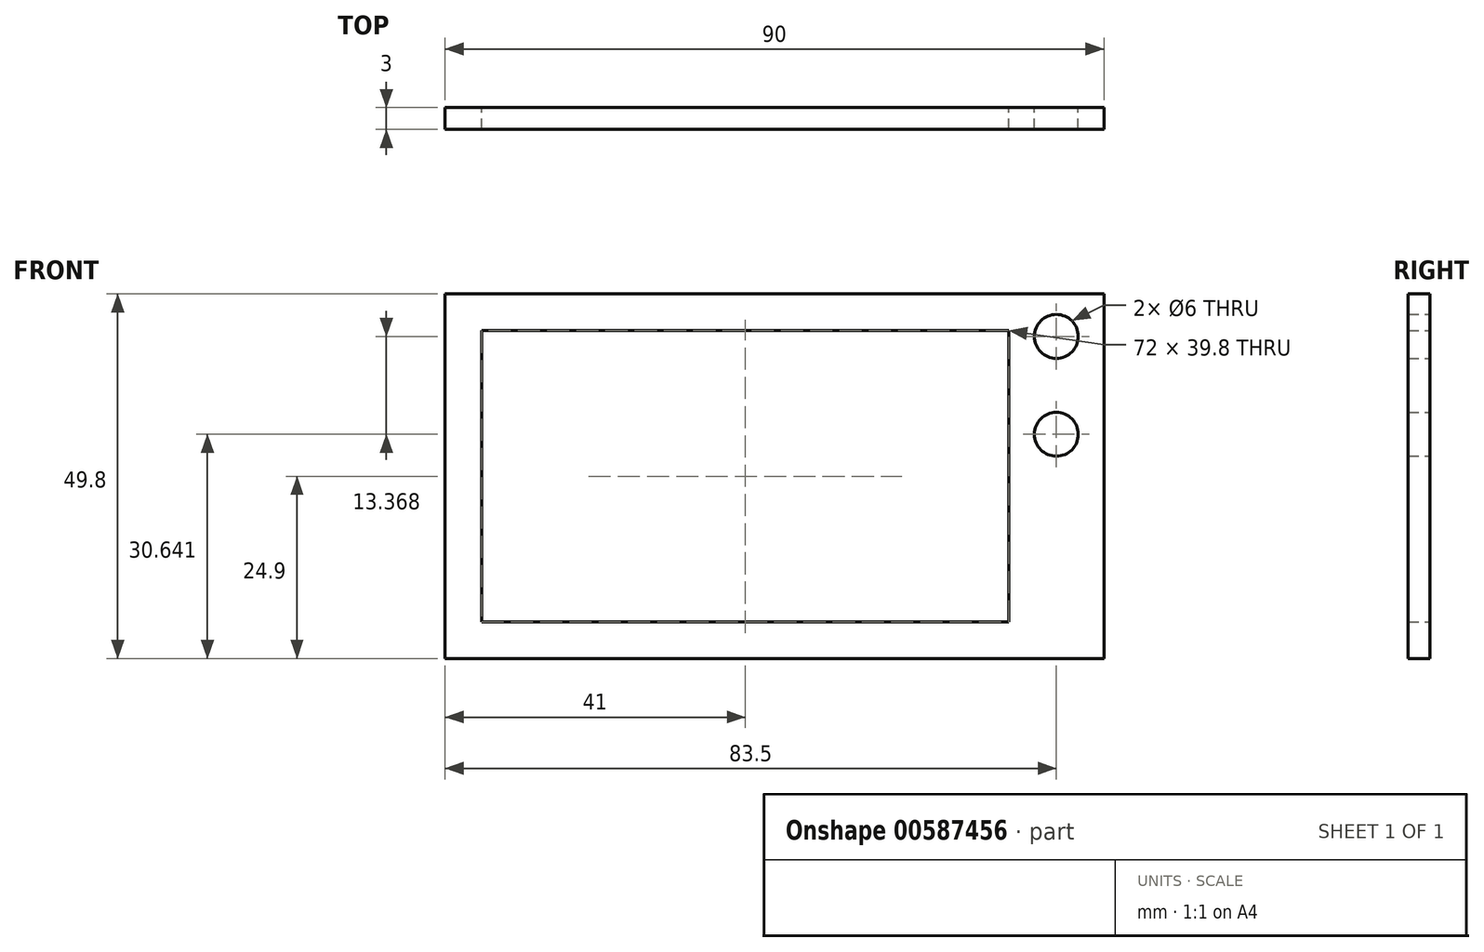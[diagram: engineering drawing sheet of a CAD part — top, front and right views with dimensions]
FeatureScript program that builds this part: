
annotation { "Feature Type Name" : "Feature", "Feature Type Description" : "" }
export const myFeature = defineFeature(function(context is Context, id is Id, definition is map)
    precondition{}
    {
        {
            var Q0;
            Q0=qCreatedBy(makeId("Front.planeOp"),FACE);
            var sketch = newSketch(context, id + "F0", { "sketchPlane" : qUnion([Q0])});
            skLineSegment(sketch, "E0", {"start": v(-45, 24.9) * mm, "end": v(-45, -24.9) * mm});
            skLineSegment(sketch, "E1", {"start": v(-45, -24.9) * mm, "end": v(45, -24.9) * mm});
            skLineSegment(sketch, "E2", {"start": v(45, -24.9) * mm, "end": v(45, 24.9) * mm});
            skLineSegment(sketch, "E3", {"start": v(45, 24.9) * mm, "end": v(-45, 24.9) * mm});
            skLineSegment(sketch, "E4", {"start": v(0, 24.9) * mm, "end": v(0, -24.9) * mm, "construction": true});
            skLineSegment(sketch, "E5", {"start": v(-45, 0) * mm, "end": v(45, 0) * mm, "construction": true});
            skCircle(sketch, "E6", {"center": v(38.5, 19.1) * mm, "radius": 3 * mm});
            skCircle(sketch, "E7", {"center": v(38.5, 5.74) * mm, "radius": 3 * mm});
            skLineSegment(sketch, "E8.bottom", {"start": v(-40, 19.9) * mm, "end": v(32, 19.9) * mm});
            skLineSegment(sketch, "E8.top", {"start": v(-40, -19.9) * mm, "end": v(32, -19.9) * mm});
            skLineSegment(sketch, "E8.left", {"start": v(-40, 19.9) * mm, "end": v(-40, -19.9) * mm});
            skLineSegment(sketch, "E8.right", {"start": v(32, 19.9) * mm, "end": v(32, -19.9) * mm});
            skSolve(sketch);
        }
        {
            var Q0;
            Q0=makeQuery(id+"F0.imprint","IMPRINT",FACE,{"disambiguationData":[TD([[makeQuery(id+"F0.imprint","IMPRINT",EDGE,{"derivedFrom":sQuery(id+"F0.wireOp",EDGE,"E0")}),1.0]])]});
            extrude(context, id + "F1", {"entities" : qUnion([Q0]), "depth" : 3 * mm, "offsetDistance" : 25 * mm});
        }
    });
